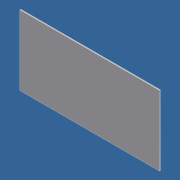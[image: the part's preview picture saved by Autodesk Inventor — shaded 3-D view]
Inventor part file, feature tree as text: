
AUTODESK INVENTOR PART (.ipt)
format: ipt  version: 2012 (Build 160160000, 160)  size: 64,000 bytes
history: native  units: in
note: dims shown in document units (in); Inventor stores cm internally (conversion verified against a paired STEP export)
features: extrude x1, sketch x1
ambient origin geometry x8: Origin, YZ Plane, XZ Plane, XY Plane, X Axis, Y Axis, Z Axis, Center Point
bodies: Solid1 (feature_tree)
feature tree (2):
  extrude  "Extrusion1"  Depth=8.0in
  sketch  "Sketch1"  dims[d0=16.0in d1=8.0in d2=0.125in d3=0.0in]
